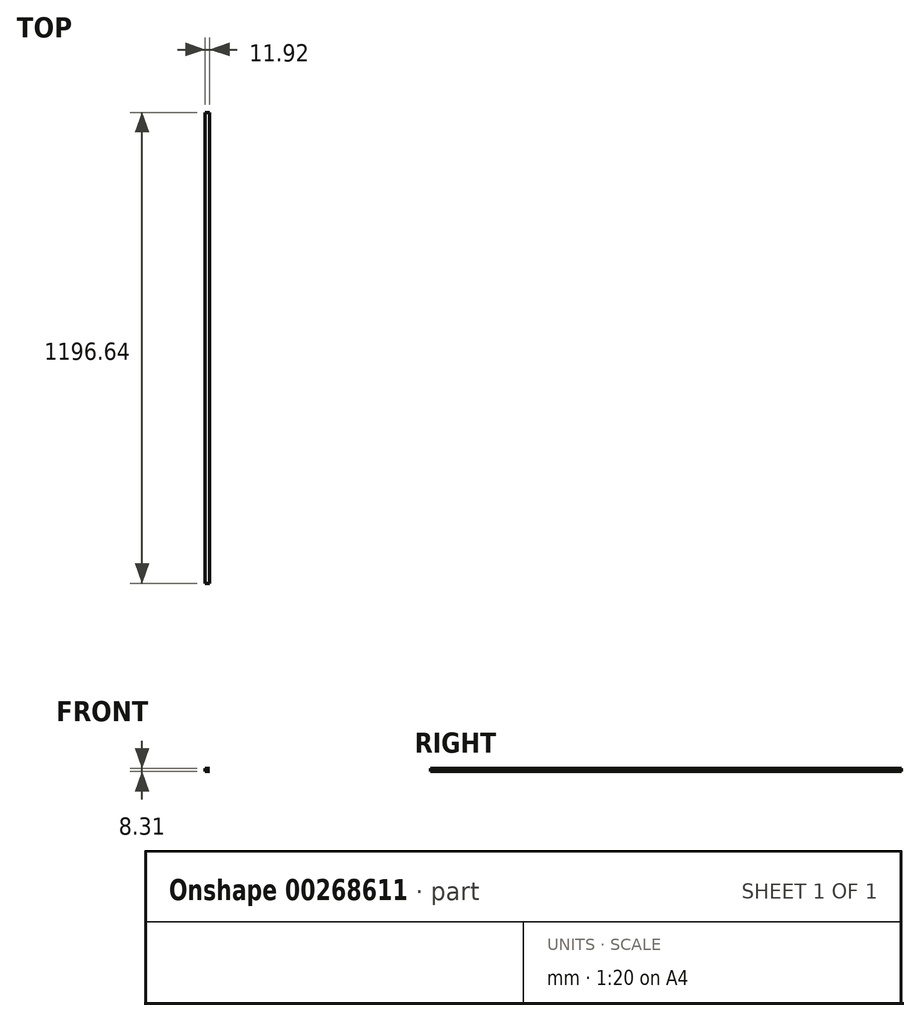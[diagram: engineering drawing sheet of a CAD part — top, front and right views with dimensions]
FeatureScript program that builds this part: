
annotation { "Feature Type Name" : "Feature", "Feature Type Description" : "" }
export const myFeature = defineFeature(function(context is Context, id is Id, definition is map)
    precondition{}
    {
        {
            var Q0;
            Q0=qCreatedBy(makeId("Front.planeOp"),FACE);
            var sketch = newSketch(context, id + "F0", { "sketchPlane" : qUnion([Q0])});
            skLineSegment(sketch, "E0.bottom", {"start": v(0, 3.35) * mm, "end": v(10.9, 3.35) * mm});
            skLineSegment(sketch, "E0.top", {"start": v(0, -3.37) * mm, "end": v(10.9, -3.37) * mm});
            skLineSegment(sketch, "E0.left", {"start": v(0, 3.35) * mm, "end": v(0, -3.37) * mm});
            skLineSegment(sketch, "E1.bottom", {"start": v(-1.02, 4.14) * mm, "end": v(10.9, 4.14) * mm});
            skLineSegment(sketch, "E1.top", {"start": v(-1.02, -4.17) * mm, "end": v(10.9, -4.17) * mm});
            skLineSegment(sketch, "E1.left", {"start": v(-1.02, 4.14) * mm, "end": v(-1.02, -4.17) * mm});
            skLineSegment(sketch, "E2", {"start": v(10.9, 3.35) * mm, "end": v(10.9, 4.14) * mm});
            skLineSegment(sketch, "E3", {"start": v(10.9, -3.37) * mm, "end": v(10.9, -4.17) * mm});
            skSolve(sketch);
        }
        {
            var Q0;
            Q0=makeQuery(id+"F0.imprint","IMPRINT",FACE,{"disambiguationData":[TD([[makeQuery(id+"F0.imprint","IMPRINT",EDGE,{"derivedFrom":sQuery(id+"F0.wireOp",EDGE,"E0.bottom")}),1.0]])]});
            extrude(context, id + "F1", {"entities" : qUnion([Q0]), "depth" : 1196.64 * mm});
        }
    });
